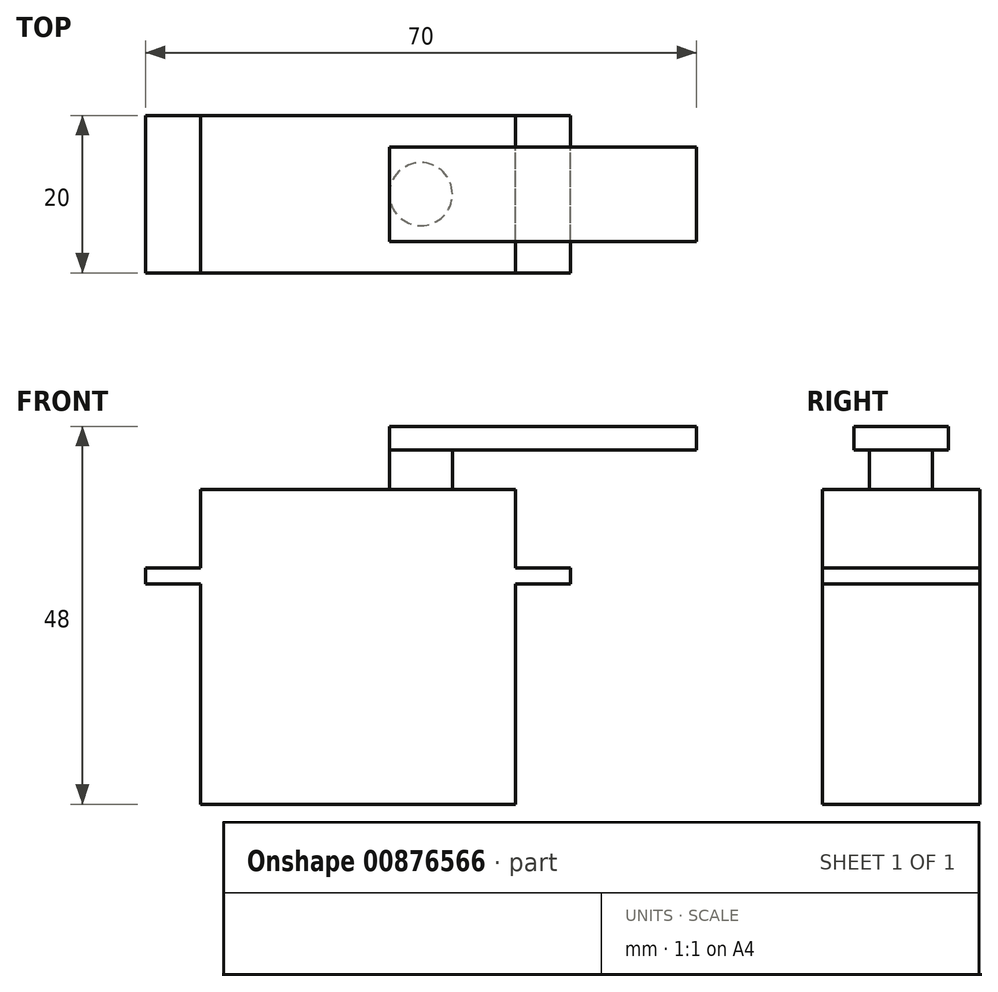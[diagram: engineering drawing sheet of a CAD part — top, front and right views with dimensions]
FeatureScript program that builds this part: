
annotation { "Feature Type Name" : "Feature", "Feature Type Description" : "" }
export const myFeature = defineFeature(function(context is Context, id is Id, definition is map)
    precondition{}
    {
        {
            var Q0;
            Q0=qCreatedBy(makeId("Front.planeOp"),FACE);
            var sketch = newSketch(context, id + "F0", { "sketchPlane" : qUnion([Q0])});
            skLineSegment(sketch, "E0.bottom", {"start": v(17.82, -20) * mm, "end": v(-22.18, -20) * mm});
            skLineSegment(sketch, "E0.top", {"start": v(17.82, 20) * mm, "end": v(-22.18, 20) * mm});
            skLineSegment(sketch, "E0.left", {"start": v(17.82, -20) * mm, "end": v(17.82, 20) * mm});
            skLineSegment(sketch, "E0.right", {"start": v(-22.18, -20) * mm, "end": v(-22.18, 20) * mm});
            skPoint(sketch, "E0.middle", {"position": v(-2.18, 0) * mm});
            skLineSegment(sketch, "E1", {"start": v(17.82, -20) * mm, "end": v(17.82, 8) * mm});
            skLineSegment(sketch, "E2.bottom", {"start": v(17.82, 8) * mm, "end": v(24.82, 8) * mm});
            skLineSegment(sketch, "E2.top", {"start": v(17.82, 10) * mm, "end": v(24.82, 10) * mm});
            skLineSegment(sketch, "E2.left", {"start": v(17.82, 8) * mm, "end": v(17.82, 10) * mm});
            skLineSegment(sketch, "E2.right", {"start": v(24.82, 8) * mm, "end": v(24.82, 10) * mm});
            skLineSegment(sketch, "E3.bottom", {"start": v(-22.18, 8) * mm, "end": v(-29.18, 8) * mm});
            skLineSegment(sketch, "E3.top", {"start": v(-22.18, 10) * mm, "end": v(-29.18, 10) * mm});
            skLineSegment(sketch, "E3.left", {"start": v(-22.18, 8) * mm, "end": v(-22.18, 10) * mm});
            skLineSegment(sketch, "E3.right", {"start": v(-29.18, 8) * mm, "end": v(-29.18, 10) * mm});
            skLineSegment(sketch, "E4", {"start": v(17.82, 20) * mm, "end": v(5.82, 20) * mm});
            skLineSegment(sketch, "E5", {"start": v(5.82, 20) * mm, "end": v(5.82, 25) * mm});
            skPoint(sketch, "E6.middle", {"position": v(5.82, 25) * mm});
            skLineSegment(sketch, "E7.bottom", {"start": v(5.82, 25) * mm, "end": v(9.82, 25) * mm});
            skLineSegment(sketch, "E7.top", {"start": v(5.82, 20) * mm, "end": v(9.82, 20) * mm});
            skLineSegment(sketch, "E7.left", {"start": v(5.82, 25) * mm, "end": v(5.82, 20) * mm});
            skLineSegment(sketch, "E7.right", {"start": v(9.82, 25) * mm, "end": v(9.82, 20) * mm});
            skLineSegment(sketch, "E8.bottom", {"start": v(5.82, 25) * mm, "end": v(40.82, 25) * mm});
            skLineSegment(sketch, "E8.top", {"start": v(5.82, 28) * mm, "end": v(40.82, 28) * mm});
            skLineSegment(sketch, "E8.left", {"start": v(5.82, 25) * mm, "end": v(5.82, 28) * mm});
            skLineSegment(sketch, "E8.right", {"start": v(40.82, 25) * mm, "end": v(40.82, 28) * mm});
            skLineSegment(sketch, "E9.bottom", {"start": v(5.82, 28) * mm, "end": v(1.82, 28) * mm});
            skLineSegment(sketch, "E9.top", {"start": v(5.82, 25) * mm, "end": v(1.82, 25) * mm});
            skLineSegment(sketch, "E9.left", {"start": v(5.82, 28) * mm, "end": v(5.82, 25) * mm});
            skLineSegment(sketch, "E9.right", {"start": v(1.82, 28) * mm, "end": v(1.82, 25) * mm});
            skSolve(sketch);
        }
        {
            var Q0;
            {var subQ7=sQuery(id+"F0.wireOp",EDGE,"E0.bottom");Q0=makeQuery(id+"F0.imprint","IMPRINT",FACE,{"disambiguationData":[TD([[makeQuery(id+"F0.imprint","IMPRINT",EDGE,{"derivedFrom":subQ7}),-1.0]])]});}
            var Q1;
            {var subQ2=sQuery(id+"F0.wireOp",EDGE,"E3.bottom");Q1=makeQuery(id+"F0.imprint","IMPRINT",FACE,{"disambiguationData":[TD([[makeQuery(id+"F0.imprint","IMPRINT",EDGE,{"derivedFrom":subQ2}),-1.0]])]});}
            var Q2;
            {var subQ2=sQuery(id+"F0.wireOp",EDGE,"E2.bottom");Q2=makeQuery(id+"F0.imprint","IMPRINT",FACE,{"disambiguationData":[TD([[makeQuery(id+"F0.imprint","IMPRINT",EDGE,{"derivedFrom":subQ2}),1.0]])]});}
            extrude(context, id + "F1", {"entities" : qUnion([Q0, Q1, Q2]), "endBound" : BoundingType.SYMMETRIC, "depth" : 20 * mm, "offsetDistance" : 25 * mm});
        }
        {
            var Q0;
            {var subQ0=sQuery(id+"F0.wireOp",EDGE,"E5");Q0=makeQuery(id+"F0.imprint","IMPRINT",FACE,{"disambiguationData":[TD([[makeQuery(id+"F0.imprint","IMPRINT",EDGE,{"derivedFrom":subQ0}),-1.0]])]});}
            var Q1;
            Q1=sQuery(id+"F0.wireOp",EDGE,"E5");
            revolve(context, id + "F2", {"operationType" : NewBodyOperationType.ADD, "surfaceOperationType" : NewSurfaceOperationType.NEW, "entities" : qUnion([Q0]), "axis" : qUnion([Q1]), "revolveType" : RevolveType.FULL});
        }
        {
            var Q0;
            Q0=makeQuery(id+"F0.imprint","IMPRINT",FACE,{"disambiguationData":[TD([[makeQuery(id+"F0.imprint","IMPRINT",EDGE,{"derivedFrom":sQuery(id+"F0.wireOp",EDGE,"E8.left")}),1.0]])]});
            var Q1;
            Q1=makeQuery(id+"F0.imprint","IMPRINT",FACE,{"disambiguationData":[TD([[makeQuery(id+"F0.imprint","IMPRINT",EDGE,{"derivedFrom":sQuery(id+"F0.wireOp",EDGE,"E7.bottom")}),1.0]])]});
            extrude(context, id + "F3", {"entities" : qUnion([Q0, Q1]), "operationType" : NewBodyOperationType.ADD, "endBound" : BoundingType.SYMMETRIC, "depth" : 12 * mm, "offsetDistance" : 25 * mm});
        }
    });
